FCSTD DOCUMENT  (FreeCAD 0.17R13509 (Git))
Label: box_culvert
License: All rights reserved
LicenseURL: http://en.wikipedia.org/wiki/All_rights_reserved
objects: Sketcher::SketchObject×4
note: 4 computed .brp shape members not serialized (recipe doc carries the construction recipe); baked Part::Feature solids carry a one-line shape summary decoded from their .brp

FEATURE [Sketcher::SketchObject] Sketch  label="box_1_cell"
  Placement = pos=(0,0,0) rot=(1,0,0;1.5708rad)
  sketch-geometry (9):
    g0: LineSegment StartX=-1828.8 StartY=2895.6 StartZ=0 EndX=1828.8 EndY=2895.6 EndZ=0
    g1: LineSegment StartX=1828.8 StartY=2895.6 StartZ=0 EndX=1828.8 EndY=457.2 EndZ=0
    g2: LineSegment StartX=1828.8 StartY=457.2 StartZ=0 EndX=-1828.8 EndY=457.2 EndZ=0
    g3: LineSegment StartX=-1828.8 StartY=457.2 StartZ=0 EndX=-1828.8 EndY=2895.6 EndZ=0
    g4: LineSegment StartX=-2082.8 StartY=3352.8 StartZ=0 EndX=2082.8 EndY=3352.8 EndZ=0
    g5: LineSegment StartX=2082.8 StartY=3352.8 StartZ=0 EndX=2082.8 EndY=0 EndZ=0
    g6: LineSegment StartX=-2082.8 StartY=0 StartZ=0 EndX=-2082.8 EndY=3352.8 EndZ=0
    g7: LineSegment StartX=-2082.8 StartY=0 StartZ=0 EndX=0 EndY=0 EndZ=0
    g8: LineSegment StartX=2082.8 StartY=0 StartZ=0 EndX=0 EndY=0 EndZ=0
  constraints (26):
    c: Coincident(g0,g1)
    c: Coincident(g1,g2)
    c: Coincident(g2,g3)
    c: Coincident(g3,g0)
    c: Horizontal(g0)
    c: Horizontal(g2)
    c: Vertical(g1)
    c: Vertical(g3)
    c: Distance(g3) = 2438.4  'Clear_Height'
    c: Distance(g0) = 3657.6  'Clear_Spen'
    c: Coincident(g4,g5)
    c: Coincident(g6,g4)
    c: Horizontal(g4)
    c: Vertical(g5)
    c: Vertical(g6)
    c: PointOnObject(g5,g-1)
    c: Coincident(g7,g6)
    c: Coincident(g7,g-1)
    c: Horizontal(g7)
    c: Coincident(g8,g5)
    c: Coincident(g8,g-1)
    c: Distance(g0,g5) = 254  'Wall_Thickness'
    c: Distance(g0,g6) = 254  '_ref_Wall_Thickness'
    c: Distance(g0,g4) = 457.2  'Top_Thickness'
    c: Distance(g1,g8) = 457.2  'Bottom_Thickness'
    c: Equal(g7,g8)
FEATURE [Sketcher::SketchObject] Sketch001  label="box_centerline"
  sketch-geometry (1):
    g0: LineSegment StartX=0 StartY=0 StartZ=0 EndX=26.5651 EndY=303.64 EndZ=0
  constraints (3):
    c: Coincident(g0,g-1)
    c: Distance(g0) = 304.8
    c: Angle(g0,g-2) = 0.0872665  'Skew'
FEATURE [Sketcher::SketchObject] Sketch002  label="headwall"
  MapMode = 1
  Placement = pos=(0,0,0) rot=(-1,0,0;4.71239rad)
  sketch-geometry (5):
    g0: LineSegment StartX=0 StartY=0 StartZ=0 EndX=1371.6 EndY=0 EndZ=0
    g1: LineSegment StartX=0 StartY=0 StartZ=0 EndX=-1371.6 EndY=0 EndZ=0
    g2: LineSegment StartX=-1371.6 StartY=0 StartZ=0 EndX=-1371.6 EndY=609.6 EndZ=0
    g3: LineSegment StartX=-1371.6 StartY=609.6 StartZ=0 EndX=1371.6 EndY=609.6 EndZ=0
    g4: LineSegment StartX=1371.6 StartY=609.6 StartZ=0 EndX=1371.6 EndY=0 EndZ=0
  constraints (14):
    c: Coincident(g0,g-1)
    c: Horizontal(g0)
    c: Coincident(g1,g-1)
    c: Horizontal(g1)
    c: Coincident(g2,g1)
    c: Coincident(g3,g2)
    c: Coincident(g4,g3)
    c: Coincident(g4,g0)
    c: Horizontal(g3)
    c: Vertical(g2)
    c: Vertical(g4)
    c: Distance(g4) = 609.6  'height'
    c: Distance(g3) = 2743.2  'width'
    c: Equal(g1,g0)
FEATURE [Sketcher::SketchObject] Sketch003  label="toewall"
  Placement = pos=(0,0,0) rot=(-1,0,0;4.71239rad)
  sketch-geometry (5):
    g0: LineSegment StartX=0 StartY=0 StartZ=0 EndX=1219.2 EndY=0 EndZ=0
    g1: LineSegment StartX=0 StartY=0 StartZ=0 EndX=-1219.2 EndY=0 EndZ=0
    g2: LineSegment StartX=-1219.2 StartY=0 StartZ=0 EndX=-1219.2 EndY=-609.6 EndZ=0
    g3: LineSegment StartX=-1219.2 StartY=-609.6 StartZ=0 EndX=1219.2 EndY=-609.6 EndZ=0
    g4: LineSegment StartX=1219.2 StartY=-609.6 StartZ=0 EndX=1219.2 EndY=0 EndZ=0
  constraints (14):
    c: Coincident(g0,g-1)
    c: Horizontal(g0)
    c: Coincident(g1,g-1)
    c: Horizontal(g1)
    c: Coincident(g2,g1)
    c: Coincident(g3,g2)
    c: Horizontal(g3)
    c: Coincident(g4,g3)
    c: Coincident(g0,g4)
    c: Vertical(g4)
    c: Vertical(g2)
    c: Equal(g1,g0)
    c: Distance(g2) = 609.6  'height'
    c: Distance(g3) = 2438.4  'width'
